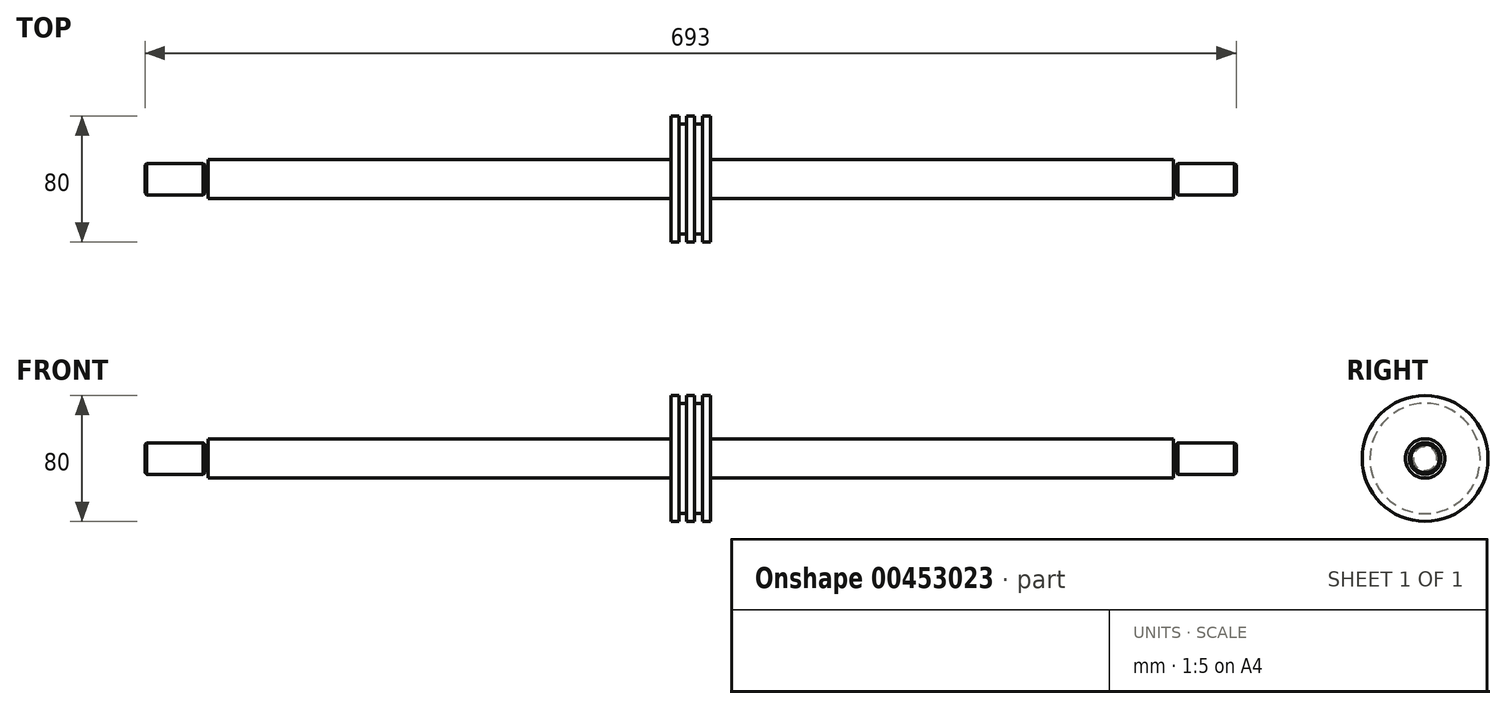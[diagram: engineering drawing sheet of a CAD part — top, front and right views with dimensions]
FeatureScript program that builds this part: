
annotation { "Feature Type Name" : "Feature", "Feature Type Description" : "" }
export const myFeature = defineFeature(function(context is Context, id is Id, definition is map)
    precondition{}
    {
        {
            var Q0;
            Q0=qCreatedBy(makeId("Front.planeOp"),FACE);
            var sketch = newSketch(context, id + "F0", { "sketchPlane" : qUnion([Q0])});
            skLineSegment(sketch, "E0.0", {"start": v(0, 12.5) * mm, "end": v(294, 12.5) * mm});
            skLineSegment(sketch, "E1", {"start": v(0, 7.5) * mm, "end": v(0, 12.5) * mm});
            skLineSegment(sketch, "E2.0", {"start": v(294, 40) * mm, "end": v(299, 40) * mm});
            skLineSegment(sketch, "E3.0", {"start": v(304, 35) * mm, "end": v(304, 40) * mm});
            skLineSegment(sketch, "E4.0", {"start": v(299, 35) * mm, "end": v(299, 40) * mm});
            skLineSegment(sketch, "E5.2", {"start": v(299, 35) * mm, "end": v(304, 35) * mm});
            skLineSegment(sketch, "E6.trimOffspring", {"start": v(304, 40) * mm, "end": v(306.5, 40) * mm});
            skLineSegment(sketch, "E7.0", {"start": v(294, 12.5) * mm, "end": v(294, 40) * mm});
            skLineSegment(sketch, "E8.0", {"start": v(-2, 7.5) * mm, "end": v(0, 7.5) * mm});
            skLineSegment(sketch, "E9.0", {"start": v(-2, 7.5) * mm, "end": v(-2, 10) * mm});
            skLineSegment(sketch, "E10.trimOffspring", {"start": v(0, 7.5) * mm, "end": v(0, 73.4) * mm, "construction": true});
            skLineSegment(sketch, "E11.0", {"start": v(-2, 10) * mm, "end": v(-40, 10) * mm});
            skLineSegment(sketch, "E12", {"start": v(-40, 10) * mm, "end": v(-40, 0) * mm});
            skLineSegment(sketch, "E13", {"start": v(-40, 0) * mm, "end": v(306.5, 0) * mm});
            skLineSegment(sketch, "E14", {"start": v(306.5, 40) * mm, "end": v(306.5, 0) * mm, "construction": true});
            skLineSegment(sketch, "E15.MirrorCS", {"start": v(314, 35) * mm, "end": v(314, 40) * mm});
            skLineSegment(sketch, "E16.MirrorCS", {"start": v(309, 35) * mm, "end": v(309, 40) * mm});
            skLineSegment(sketch, "E17.MirrorCS", {"start": v(613, 7.5) * mm, "end": v(613, 12.5) * mm});
            skLineSegment(sketch, "E18.MirrorCS", {"start": v(319, 40) * mm, "end": v(314, 40) * mm});
            skLineSegment(sketch, "E19.MirrorCS", {"start": v(615, 7.5) * mm, "end": v(613, 7.5) * mm});
            skLineSegment(sketch, "E20.MirrorCS", {"start": v(615, 7.5) * mm, "end": v(615, 10) * mm});
            skLineSegment(sketch, "E21.MirrorCS", {"start": v(309, 40) * mm, "end": v(306.5, 40) * mm});
            skLineSegment(sketch, "E22.MirrorCS", {"start": v(314, 35) * mm, "end": v(309, 35) * mm});
            skLineSegment(sketch, "E23.MirrorCS", {"start": v(653, 10) * mm, "end": v(653, 0) * mm});
            skLineSegment(sketch, "E24.MirrorCS", {"start": v(613, 12.5) * mm, "end": v(319, 12.5) * mm});
            skLineSegment(sketch, "E25.MirrorCS", {"start": v(653, 0) * mm, "end": v(306.5, 0) * mm});
            skLineSegment(sketch, "E26.MirrorCS", {"start": v(615, 10) * mm, "end": v(653, 10) * mm});
            skLineSegment(sketch, "E27.MirrorCS", {"start": v(319, 12.5) * mm, "end": v(319, 40) * mm});
            skSolve(sketch);
        }
        {
            var Q0;
            Q0=makeQuery(id+"F0.imprint","IMPRINT",FACE,{"disambiguationData":[TD([[makeQuery(id+"F0.imprint","IMPRINT",EDGE,{"derivedFrom":sQuery(id+"F0.wireOp",EDGE,"E0.0")}),-1.0]])]});
            var Q1;
            Q1=sQuery(id+"F0.wireOp",EDGE,"E13");
            revolve(context, id + "F1", {"entities" : qUnion([Q0]), "axis" : qUnion([Q1]), "revolveType" : RevolveType.FULL});
        }
        {
            var Q0;
            Q0=makeQuery(id+"F1.opRevolve","SWEPT_EDGE",EDGE,{"disambiguationData":[OSD([sQuery(id+"F0.wireOp",EDGE,"E23.MirrorCS"),sQuery(id+"F0.wireOp",EDGE,"E26.MirrorCS")])]});
            var Q1;
            Q1=makeQuery(id+"F1.opRevolve","SWEPT_EDGE",EDGE,{"disambiguationData":[OSD([sQuery(id+"F0.wireOp",EDGE,"E20.MirrorCS"),sQuery(id+"F0.wireOp",EDGE,"E26.MirrorCS")])]});
            var Q2;
            Q2=makeQuery(id+"F1.opRevolve","SWEPT_EDGE",EDGE,{"disambiguationData":[OSD([sQuery(id+"F0.wireOp",EDGE,"E11.0"),sQuery(id+"F0.wireOp",EDGE,"E12")])]});
            var Q3;
            Q3=makeQuery(id+"F1.opRevolve","SWEPT_EDGE",EDGE,{"disambiguationData":[OSD([sQuery(id+"F0.wireOp",EDGE,"E9.0"),sQuery(id+"F0.wireOp",EDGE,"E11.0")])]});
            chamfer(context, id + "F2", {"entities" : qUnion([Q0, Q1, Q2, Q3]), "width" : 1 * mm, "tangentPropagation" : true});
        }
    });
